# Revit family: Franke_A200_MS_EC_FW(USA)
name_source: partatom
category: Specialty Equipment
revit_build: Autodesk Revit 2015 (Build: 20140606_1530(x64)
units: mm (PartAtom-declared; Revit-internal decimal feet)

## types (2) — shared parameters
Assembly Code = fully automatic coffee machine
Cycle (A200) = 60 Hz
Cycle Alternative (A200) = 0 Hz
Depth (mm) = 560 mm  [stored 1.83727 ft]
Description = A200 fully automatic coffee machine
Energy loss acc. to DIN 18873(A200) = 0.761 kWh/24 h - 230 V
Height (mm) = 604 mm  [stored 1.98163 ft]
Incoming water (cold water) = 8 mm  [stored 0.0262467 ft]
Keynote = fully automatic coffee machine
Manufacturer = Franke
Max Overcurrent Protection (A200) = 15 A
Model = 410914 - A200 MS EC FW
Noise emission = 70 dB
Number of Nutral Conductors (A200) = -
Number of Poles (A200) = 2
Number of Protective Conductors (A200) = 1
URL = https://www.franke.com
Volts max. (A200) = 0 V
Volts min. (A200) = 120 V
Wastewater = 16 mm  [stored 0.0524934 ft]
Water pressure = 800000.0 Pa
Water pressure (with filter) = 600000.0 Pa
Watts max. (A200) = 0 W
Watts min. (A200) = 1450 W
Weight = 25 kg
Width (mm) = 340 mm  [stored 1.11549 ft]
zero-valued in all types: Cost

## per-type parameters (varying)
| type | Frontcover |
| A200 MS EC FW(120V/black line/USA) | Franke Black |
| A200 MS EC FW(120V/anthracite/USA) | Franke Anthracite |

note: [stored X ft] marks values corroborated as IEEE doubles in the binary element streams (Revit-internal decimal feet)

## geometry (parser evidence)
native form markers: Extrusion x1
no freeform markers — native parametric forms only
